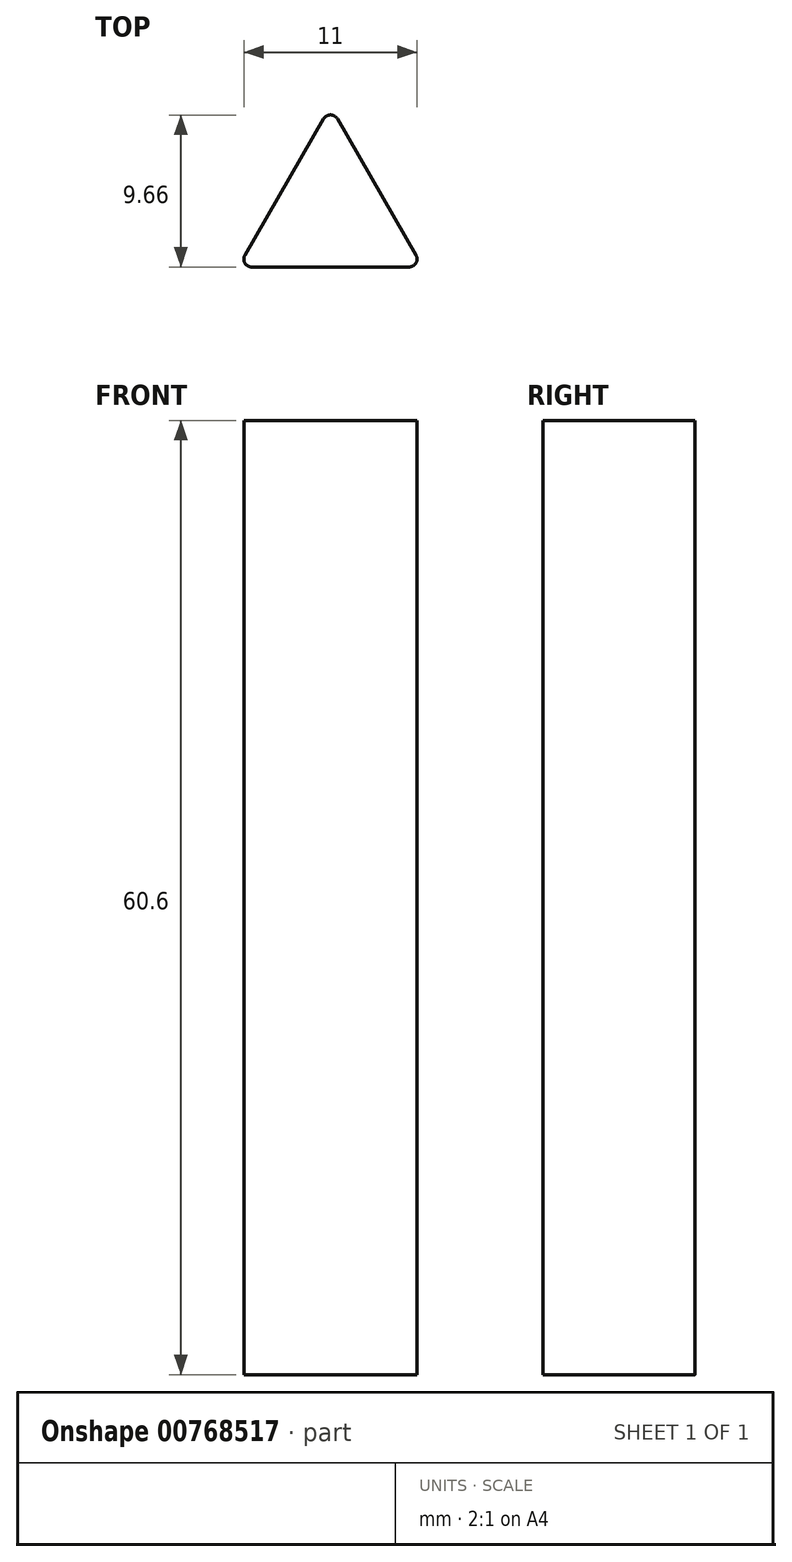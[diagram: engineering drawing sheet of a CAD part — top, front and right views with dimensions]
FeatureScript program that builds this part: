
annotation { "Feature Type Name" : "Feature", "Feature Type Description" : "" }
export const myFeature = defineFeature(function(context is Context, id is Id, definition is map)
    precondition{}
    {
        {
            var Q0;
            Q0=qCreatedBy(makeId("Top.planeOp"),FACE);
            var sketch = newSketch(context, id + "F0", { "sketchPlane" : qUnion([Q0])});
            skCircle(sketch, "E0.cCircle", {"center": v(0, 0) * mm, "radius": 6.77 * mm, "construction": true});
            skLineSegment(sketch, "E0.0", {"start": v(0.43, 6.02) * mm, "end": v(5.43, -2.64) * mm});
            skLineSegment(sketch, "E0.1", {"start": v(5, -3.39) * mm, "end": v(-5, -3.39) * mm});
            skLineSegment(sketch, "E0.2", {"start": v(-5.43, -2.64) * mm, "end": v(-0.43, 6.02) * mm});
            skPoint(sketch, "E1.visualSharp", {"position": v(0, 6.77) * mm});
            skArc(sketch, "E1.filletArc", {"start": v(0.43, 6.02) * mm, "mid": v(0, 6.27) * mm, "end": v(-0.43, 6.02) * mm});
            skPoint(sketch, "E2.visualSharp", {"position": v(5.87, -3.39) * mm});
            skArc(sketch, "E2.filletArc", {"start": v(5, -3.39) * mm, "mid": v(5.43, -3.14) * mm, "end": v(5.43, -2.64) * mm});
            skPoint(sketch, "E3.visualSharp", {"position": v(-5.87, -3.39) * mm});
            skArc(sketch, "E3.filletArc", {"start": v(-5.43, -2.64) * mm, "mid": v(-5.43, -3.14) * mm, "end": v(-5, -3.39) * mm});
            skSolve(sketch);
        }
        {
            var Q0;
            Q0=makeQuery(id+"F0.imprint","IMPRINT",FACE,{"disambiguationData":[TD([[makeQuery(id+"F0.imprint","IMPRINT",EDGE,{"derivedFrom":sQuery(id+"F0.wireOp",EDGE,"E0.0")}),-1.0]])]});
            extrude(context, id + "F1", {"entities" : qUnion([Q0]), "oppositeDirection" : true, "depth" : 60.6 * mm, "offsetDistance" : 25 * mm});
        }
    });
